# Revit family: Pump_Commercial-Effluent-Zoeller-6400_Series
name_source: partatom
category: Mechanical Equipment
units: mm (PartAtom-declared; Revit-internal decimal feet)

## family parameters
Always vertical = No
Cut with Voids When Loaded = No
OmniClass Number = 23.60.30.21
OmniClass Title = Pumps
Part Type = Normal
Room Calculation Point = No
Round Connector Dimension = Use Radius
Shared = Yes
Work Plane-Based = Yes

## types (2) — shared parameters
Assembly Code = D2010900
Default Elevation = 0"
Description = Commercial Effluent Pumps
Discharge Diameter = 4"
Discharge Height = 6 1/2"
Discharge Radius = 2"
Finish = Cast Iron-Zoeller-Powder Coated Epoxy
Height = 27 1/2"
Hertz = 60
Impeller Type = Cast Iron Vortex
Installation Type = Floor Mounted
Insulation = Class B
Lead Wires Insulation = Class B
Length = 16 1/8"
Locked Rotor Amps (Voltage Dependant) = 17.9 - 49.5
Manufacturer = Zoeller
Material = Cast Iron-Zoeller-Powder Coated Epoxy
Max. Stator Temp. = 266 °F
Max. Water Temp. = 130 °F
Min. Recommended Fluid Level = 12"
Minimum Head = 60"
Moisture Sensor (Optional) = Moisture Sensing Probes (Requires a circuit in control panel)
Motor Design Letter = NEMA B
Motor Shaft = 416 S.S.
Motor Thermal Shutoff (Single Phase Only) = Thermal Overload With Automatic Reset
Motor Type = Submersible
O-Rings and Cover Gasket = Viton
Operation = Non-Automatic
Phase = 1 or 3
Price = Prices may vary. Please consult Manufacturer Representative for most up-to-date price list.
Product Documentation Link = https://www.zoellerengineered.com
Product Page URL = https://www.zoellerengineered.com
RPM = 1750
Revised Date = 03/01/2023
Service Factor = 1.15
Shaft Seal Lower (Options) = Silicon Carbide/Silicon Carbide
Shaft Seal Lower Standard = Silicon Carbide/Carbon
Shaft Seal Upper (Options) = Silicon Carbide/Carbon, Silicon Carbide/Silicon Carbide
Shaft Seal Upper Standard = Carbon/Ceramic
Shipping Weight = 150 lbs (68 kg)
Type = Permanent Split Capacitor or 3 Phase
Type SOW Power Cord Length = 300"
URL = https://www.zoellerengineered.com
Voltage = 230/460
Warranty Information = 36 Months (Limited)
Waste Connection = Yes
Width = 12 1/2"

## per-type parameters (varying)
| type | Full Load Amps (Voltage Dependent) | Max Flow @ 5' | Maximum Head | Motor |
| 6404-4" | 4.1 - 14.4 | 300 GPM | 396" | 2 HP |
| 6405-4" | 4.8 - 20.2 | 361 GPM | 456" | 3 HP |

note: column(s) folded — value = type name in every type: Model

## geometry (parser evidence)
native form markers: Sweep x2
no freeform markers — native parametric forms only
